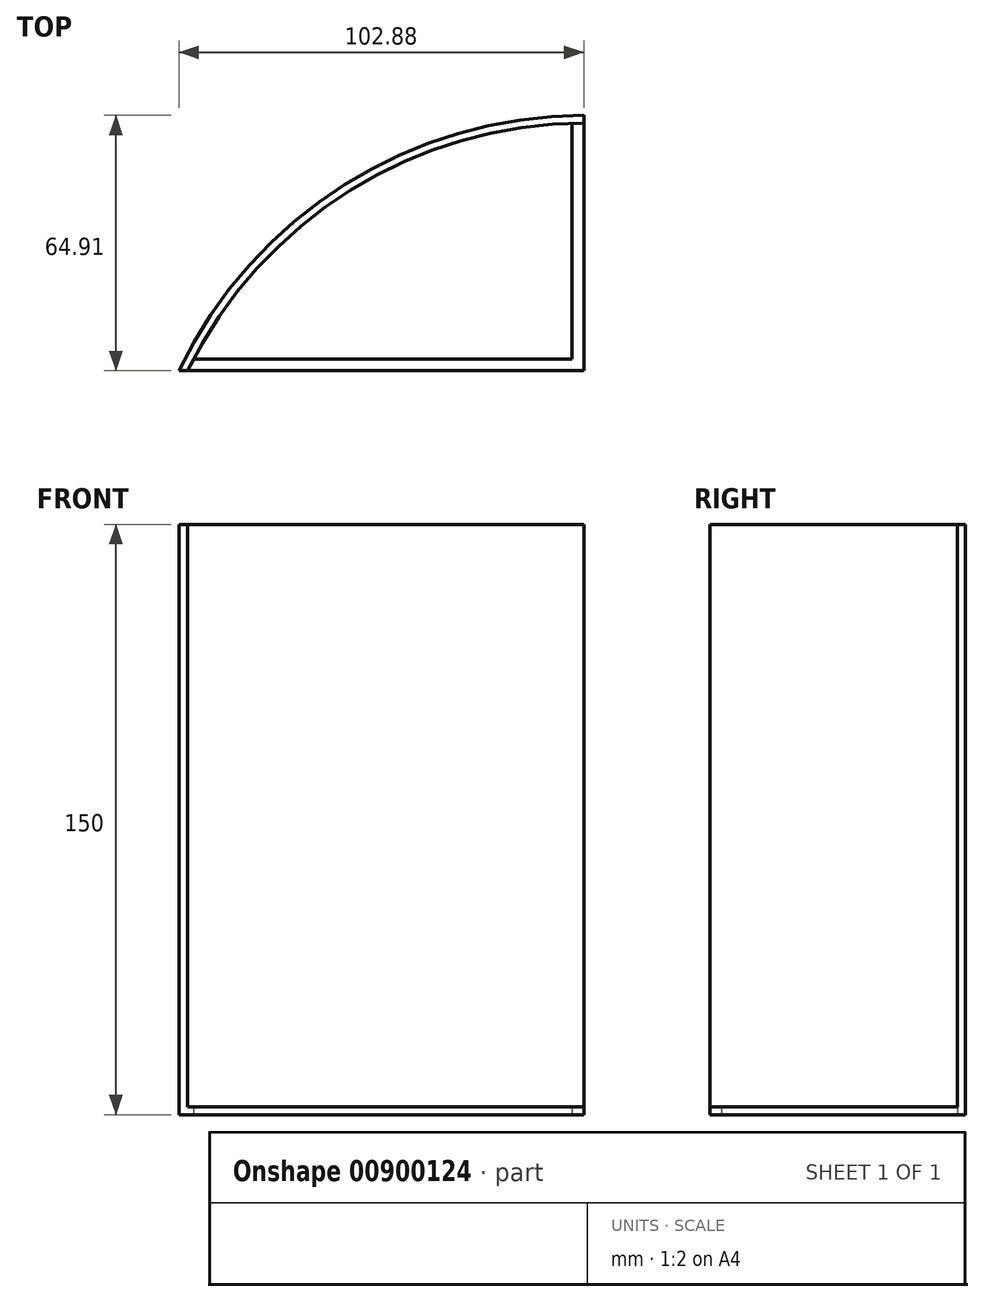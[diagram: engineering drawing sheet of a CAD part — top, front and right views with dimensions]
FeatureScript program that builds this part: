
annotation { "Feature Type Name" : "Feature", "Feature Type Description" : "" }
export const myFeature = defineFeature(function(context is Context, id is Id, definition is map)
    precondition{}
    {
        {
            var Q0;
            Q0=qCreatedBy(makeId("Top.planeOp"),FACE);
            var sketch = newSketch(context, id + "F0", { "sketchPlane" : qUnion([Q0])});
            skCircle(sketch, "E0", {"center": v(0.2, -49.39) * mm, "radius": 114.3 * mm});
            skPoint(sketch, "E0.first.point", {"position": v(103.28, 0) * mm});
            skPoint(sketch, "E0.second.point", {"position": v(-106.3, -90.9) * mm});
            skPoint(sketch, "E0.third.point", {"position": v(-102.88, 0) * mm});
            skCircle(sketch, "E1.0", {"center": v(0.2, -49.39) * mm, "radius": 112.3 * mm});
            skLineSegment(sketch, "E2", {"start": v(0, 0) * mm, "end": v(-102.88, 0) * mm});
            skLineSegment(sketch, "E3.MirrorCS", {"start": v(0, 0) * mm, "end": v(102.88, 0) * mm});
            skLineSegment(sketch, "E4.0", {"start": v(0, 3) * mm, "end": v(-101.39, 3) * mm});
            skLineSegment(sketch, "E5.MirrorCS", {"start": v(0, 3) * mm, "end": v(101.39, 3) * mm});
            skLineSegment(sketch, "E6", {"start": v(0, 64.91) * mm, "end": v(0, 0) * mm});
            skLineSegment(sketch, "E7.0", {"start": v(-3, 64.45) * mm, "end": v(-3, 0) * mm});
            skSolve(sketch);
        }
        {
            var Q0;
            {var subQ0=sQuery(id+"F0.wireOp",EDGE,"E2");var subQ1=sQuery(id+"F0.wireOp",EDGE,"E0");var subQ2=makeQuery(id+"F0.imprint","INTERSECT",VERTEX,{"derivedFrom":[subQ1,subQ0]});Q0=makeQuery(id+"F0.imprint","IMPRINT",FACE,{"disambiguationData":[TD([[makeQuery(id+"F0.imprint","IMPRINT",EDGE,{"disambiguationData":[TD([[subQ2,1.0]])],"derivedFrom":subQ1}),1.0]])]});}
            var Q1;
            {var subQ2=sQuery(id+"F0.wireOp",EDGE,"E4.0");var subQ5=sQuery(id+"F0.wireOp",EDGE,"E0");var subQ8=makeQuery(id+"F0.imprint","INTERSECT",VERTEX,{"derivedFrom":[subQ5,subQ2]});Q1=makeQuery(id+"F0.imprint","IMPRINT",FACE,{"disambiguationData":[TD([[makeQuery(id+"F0.imprint","IMPRINT",EDGE,{"disambiguationData":[TD([[subQ8,1.0]])],"derivedFrom":subQ5}),1.0]])]});}
            extrude(context, id + "F1", {"entities" : qUnion([Q0, Q1]), "depth" : 150 * mm, "offsetDistance" : 25 * mm});
        }
        {
            var Q0;
            {var subQ0=sQuery(id+"F0.wireOp",EDGE,"E4.0");var subQ1=sQuery(id+"F0.wireOp",EDGE,"E1.0");var subQ2=makeQuery(id+"F0.imprint","INTERSECT",VERTEX,{"derivedFrom":[subQ1,subQ0]});Q0=makeQuery(id+"F0.imprint","IMPRINT",FACE,{"disambiguationData":[TD([[makeQuery(id+"F0.imprint","IMPRINT",EDGE,{"disambiguationData":[TD([[subQ2,-1.0]])],"derivedFrom":subQ1}),1.0]])]});}
            var Q1;
            {var subQ1=sQuery(id+"F0.wireOp",EDGE,"E2");var subQ3=sQuery(id+"F0.wireOp",EDGE,"E7.0");var subQ4=makeQuery(id+"F0.imprint","INTERSECT",VERTEX,{"derivedFrom":[subQ1,subQ3]});Q1=makeQuery(id+"F0.imprint","IMPRINT",FACE,{"disambiguationData":[TD([[makeQuery(id+"F0.imprint","IMPRINT",EDGE,{"disambiguationData":[TD([[subQ4,1.0]])],"derivedFrom":subQ3}),1.0]])]});}
            var Q2;
            {var subQ0=sQuery(id+"F0.wireOp",EDGE,"E7.0");var subQ1=sQuery(id+"F0.wireOp",EDGE,"E1.0");var subQ2=makeQuery(id+"F0.imprint","INTERSECT",VERTEX,{"derivedFrom":[subQ1,subQ0]});Q2=makeQuery(id+"F0.imprint","IMPRINT",FACE,{"disambiguationData":[TD([[makeQuery(id+"F0.imprint","IMPRINT",EDGE,{"disambiguationData":[TD([[subQ2,1.0]])],"derivedFrom":subQ1}),1.0]])]});}
            extrude(context, id + "F2", {"entities" : qUnion([Q0, Q1, Q2]), "operationType" : NewBodyOperationType.ADD, "depth" : 2 * mm, "offsetDistance" : 25 * mm});
        }
    });
